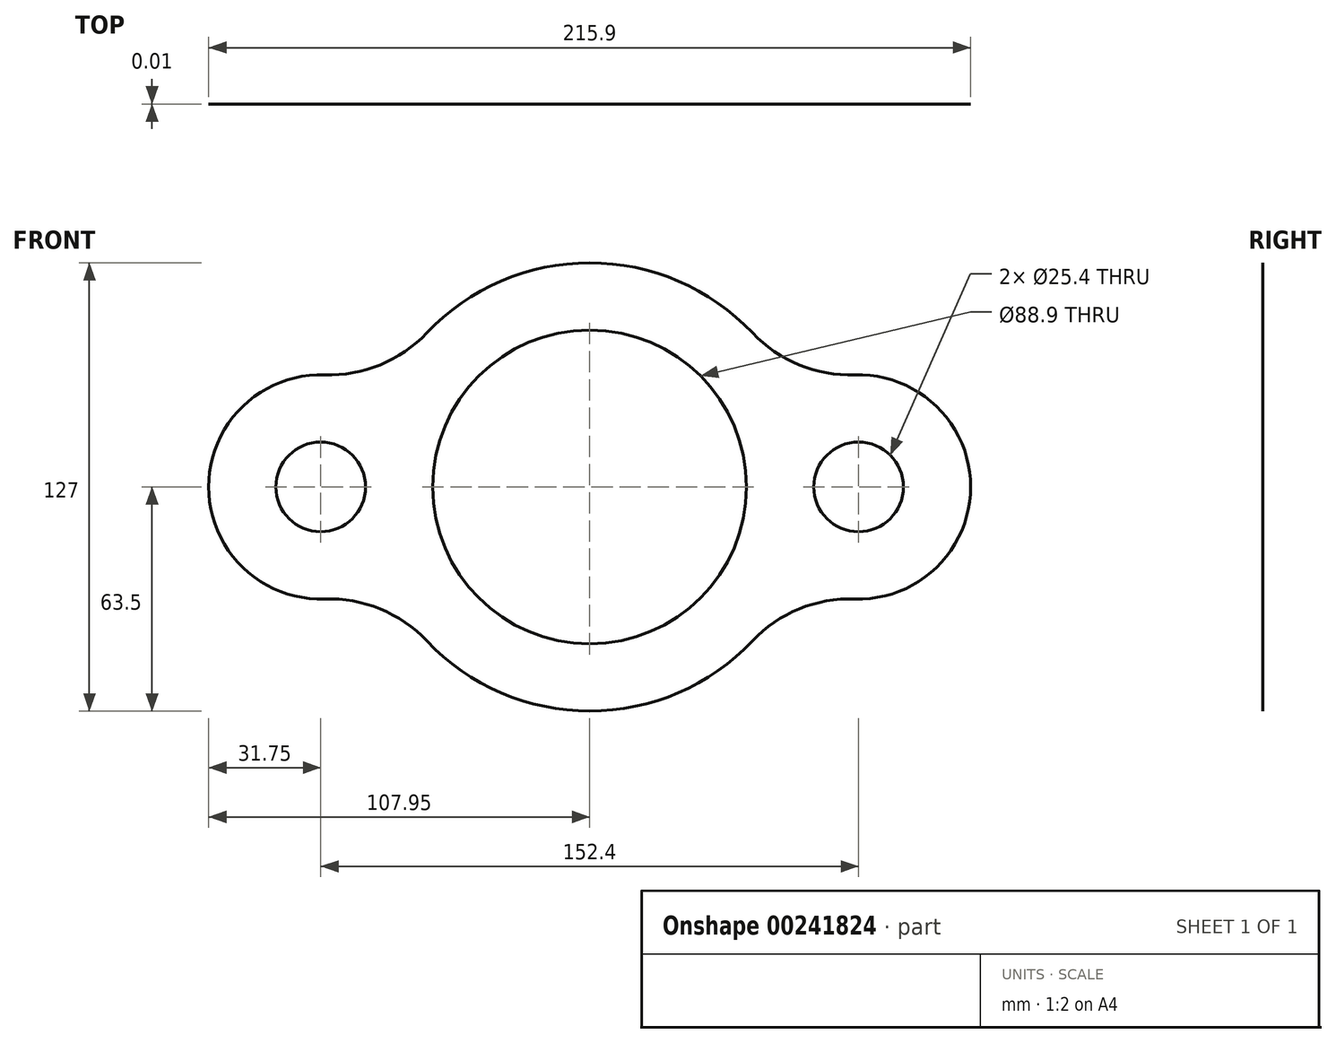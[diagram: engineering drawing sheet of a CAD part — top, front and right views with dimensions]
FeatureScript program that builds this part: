
annotation { "Feature Type Name" : "Feature", "Feature Type Description" : "" }
export const myFeature = defineFeature(function(context is Context, id is Id, definition is map)
    precondition{}
    {
        {
            var Q0;
            Q0=qCreatedBy(makeId("Front.planeOp"),FACE);
            var sketch = newSketch(context, id + "F0", { "sketchPlane" : qUnion([Q0])});
            skCircle(sketch, "E0", {"center": v(-76.2, 0) * mm, "radius": 12.7 * mm});
            skCircle(sketch, "E1", {"center": v(76.2, 0) * mm, "radius": 12.7 * mm});
            skArc(sketch, "E2", {"start": v(75.12, -31.73) * mm, "mid": v(107.95, 0) * mm, "end": v(75.12, 31.73) * mm});
            skArc(sketch, "E3", {"start": v(-75.12, 31.73) * mm, "mid": v(-107.95, 0) * mm, "end": v(-75.12, -31.73) * mm});
            skCircle(sketch, "E4", {"center": v(0, 0) * mm, "radius": 44.45 * mm});
            skArc(sketch, "E5.trimOffspring", {"start": v(46.14, 43.63) * mm, "mid": v(0, 63.5) * mm, "end": v(-46.14, 43.63) * mm});
            skPoint(sketch, "E6.visualSharp", {"position": v(-57.94, 25.98) * mm});
            skArc(sketch, "E6.filletArc", {"start": v(-75.12, 31.73) * mm, "mid": v(-59.35, 34.56) * mm, "end": v(-46.14, 43.63) * mm});
            skPoint(sketch, "E7.visualSharp", {"position": v(57.94, 25.98) * mm});
            skArc(sketch, "E7.filletArc", {"start": v(46.14, 43.63) * mm, "mid": v(59.35, 34.56) * mm, "end": v(75.12, 31.73) * mm});
            skArc(sketch, "E8", {"start": v(-46.14, -43.63) * mm, "mid": v(0, -63.5) * mm, "end": v(46.14, -43.63) * mm});
            skPoint(sketch, "E9.visualSharp", {"position": v(-57.94, -25.98) * mm});
            skArc(sketch, "E9.filletArc", {"start": v(-46.14, -43.63) * mm, "mid": v(-59.35, -34.56) * mm, "end": v(-75.12, -31.73) * mm});
            skPoint(sketch, "E10.visualSharp", {"position": v(57.94, -25.98) * mm});
            skArc(sketch, "E10.filletArc", {"start": v(75.12, -31.73) * mm, "mid": v(59.35, -34.56) * mm, "end": v(46.14, -43.63) * mm});
            skLineSegment(sketch, "E11", {"start": v(-76.2, 0) * mm, "end": v(76.2, 0) * mm, "construction": true});
            skSolve(sketch);
        }
        {
            var Q0;
            Q0=makeQuery(id+"F0.imprint","IMPRINT",FACE,{"disambiguationData":[TD([[makeQuery(id+"F0.imprint","IMPRINT",EDGE,{"derivedFrom":sQuery(id+"F0.wireOp",EDGE,"E0")}),-1.0]])]});
            extrude(context, id + "F1", {"entities" : qUnion([Q0]), "depth" : 1 / 101.6 * mm});
        }
    });
